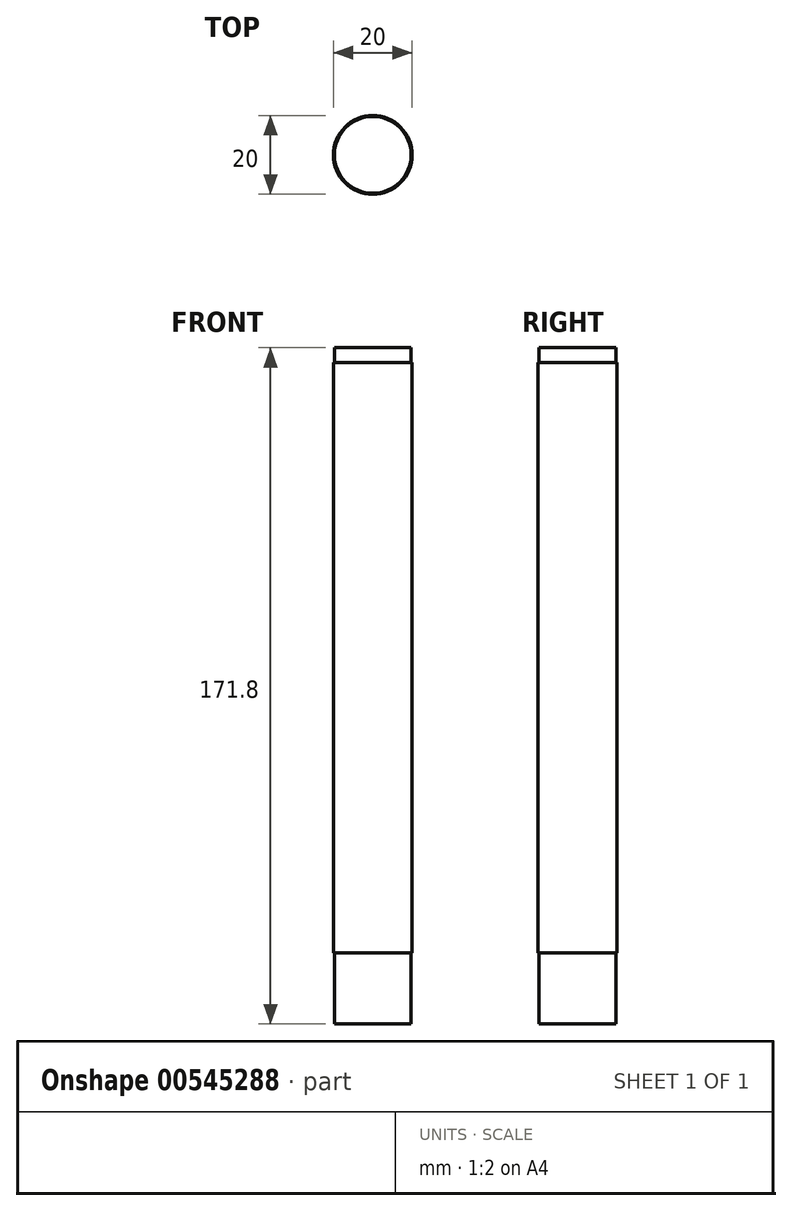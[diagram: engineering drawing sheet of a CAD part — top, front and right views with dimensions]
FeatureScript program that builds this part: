
annotation { "Feature Type Name" : "Feature", "Feature Type Description" : "" }
export const myFeature = defineFeature(function(context is Context, id is Id, definition is map)
    precondition{}
    {
        {
            var Q0;
            Q0=qCreatedBy(makeId("Top.planeOp"),FACE);
            var sketch = newSketch(context, id + "F0", { "sketchPlane" : qUnion([Q0])});
            skCircle(sketch, "E0", {"center": v(0, 0) * mm, "radius": 10 * mm});
            skSolve(sketch);
        }
        {
            var Q0;
            Q0=makeQuery(id+"F0.imprint","IMPRINT",FACE,{"disambiguationData":[TD([[makeQuery(id+"F0.imprint","IMPRINT",EDGE,{"derivedFrom":sQuery(id+"F0.wireOp",EDGE,"E0")}),1.0]])]});
            extrude(context, id + "F1", {"entities" : qUnion([Q0]), "depth" : 150 * mm, "offsetDistance" : 25 * mm});
        }
        {
            var Q0;
            Q0=qCreatedBy(makeId("Top.planeOp"),FACE);
            var sketch = newSketch(context, id + "F2", { "sketchPlane" : qUnion([Q0])});
            skCircle(sketch, "E1", {"center": v(0, 0) * mm, "radius": 9.75 * mm});
            skSolve(sketch);
        }
        {
            var Q0;
            Q0=makeQuery(id+"F2.imprint","IMPRINT",FACE,{"disambiguationData":[TD([[makeQuery(id+"F2.imprint","IMPRINT",EDGE,{"derivedFrom":sQuery(id+"F2.wireOp",EDGE,"E1")}),1.0]])]});
            extrude(context, id + "F3", {"entities" : qUnion([Q0]), "operationType" : NewBodyOperationType.ADD, "depth" : 153.7 * mm, "offsetDistance" : 25 * mm, "hasSecondDirection" : true, "secondDirectionOppositeDirection" : true, "secondDirectionDepth" : 18.1 * mm});
        }
    });
